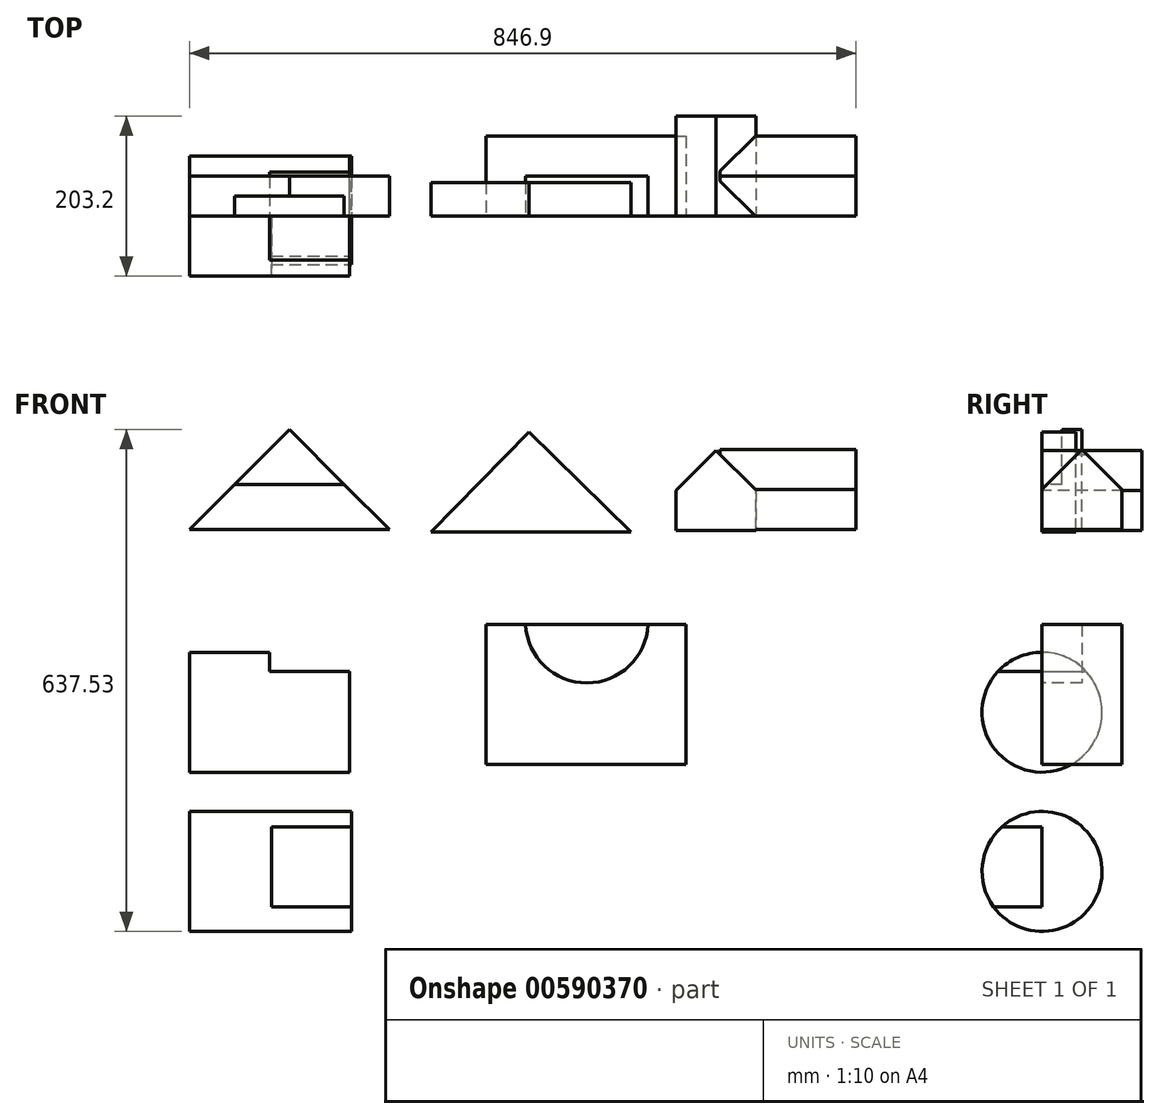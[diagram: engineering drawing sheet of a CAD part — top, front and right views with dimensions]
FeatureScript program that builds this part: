
annotation { "Feature Type Name" : "Feature", "Feature Type Description" : "" }
export const myFeature = defineFeature(function(context is Context, id is Id, definition is map)
    precondition{}
    {
        {
            var Q0;
            Q0=qCreatedBy(makeId("Front.planeOp"),FACE);
            var sketch = newSketch(context, id + "F0", { "sketchPlane" : qUnion([Q0])});
            skLineSegment(sketch, "E0", {"start": v(0, 0) * mm, "end": v(254, 0) * mm});
            skLineSegment(sketch, "E1", {"start": v(254, 0) * mm, "end": v(127, 127) * mm});
            skLineSegment(sketch, "E2", {"start": v(0, 0) * mm, "end": v(127, 127) * mm});
            skSolve(sketch);
        }
        {
            var Q0;
            Q0=makeQuery(id+"F0.imprint","IMPRINT",FACE,{"disambiguationData":[TD([[makeQuery(id+"F0.imprint","IMPRINT",EDGE,{"derivedFrom":sQuery(id+"F0.wireOp",EDGE,"E0")}),1.0]])]});
            extrude(context, id + "F1", {"entities" : qUnion([Q0]), "oppositeDirection" : true, "depth" : 50.8 * mm, "offsetDistance" : 25.4 * mm});
        }
        {
            var Q0;
            Q0=makeQuery(id+"F1.opExtrude","CAP_FACE",FACE,{"disambiguationData":[OSD([sQuery(id+"F0.wireOp",EDGE,"E0"),sQuery(id+"F0.wireOp",EDGE,"E1"),sQuery(id+"F0.wireOp",EDGE,"E2")])],"isStart":true});
            var sketch = newSketch(context, id + "F2", { "sketchPlane" : qUnion([Q0])});
            skLineSegment(sketch, "E3", {"start": v(57.32, 57.32) * mm, "end": v(196.68, 57.32) * mm});
            skSolve(sketch);
        }
        {
            var Q0;
            {var subQ0=sQuery(id+"F2.wireOp",EDGE,"E3");Q0=makeQuery(id+"F2.imprint","IMPRINT",FACE,{"disambiguationData":[TD([[makeQuery(id+"F2.imprint","IMPRINT",EDGE,{"derivedFrom":subQ0}),1.0]])]});}
            extrude(context, id + "F3", {"entities" : qUnion([Q0]), "operationType" : NewBodyOperationType.REMOVE, "oppositeDirection" : true, "depth" : 25.4 * mm, "offsetDistance" : 25.4 * mm});
        }
        {
            var Q0;
            Q0=qCreatedBy(makeId("Front.planeOp"),FACE);
            var sketch = newSketch(context, id + "F4", { "sketchPlane" : qUnion([Q0])});
            skLineSegment(sketch, "E4", {"start": v(307.02, -3.1) * mm, "end": v(561.02, -3.1) * mm});
            skLineSegment(sketch, "E5", {"start": v(307.02, -3.1) * mm, "end": v(431.46, 123.9) * mm});
            skLineSegment(sketch, "E6", {"start": v(561.02, -3.1) * mm, "end": v(431.46, 123.9) * mm});
            skSolve(sketch);
        }
        {
            var Q0;
            Q0=makeQuery(id+"F4.imprint","IMPRINT",FACE,{"disambiguationData":[TD([[makeQuery(id+"F4.imprint","IMPRINT",EDGE,{"derivedFrom":sQuery(id+"F4.wireOp",EDGE,"E4")}),1.0]])]});
            extrude(context, id + "F5", {"entities" : qUnion([Q0]), "oppositeDirection" : true, "depth" : 42.67 * mm, "offsetDistance" : 25.4 * mm});
        }
        {
            var Q0;
            Q0=qCreatedBy(makeId("Front.planeOp"),FACE);
            var sketch = newSketch(context, id + "F6", { "sketchPlane" : qUnion([Q0])});
            skLineSegment(sketch, "E7", {"start": v(618.3, -0.96) * mm, "end": v(618.3, 49.84) * mm});
            skLineSegment(sketch, "E8", {"start": v(618.3, 49.84) * mm, "end": v(669.1, 100.64) * mm});
            skLineSegment(sketch, "E9", {"start": v(669.1, 100.64) * mm, "end": v(719.9, 49.84) * mm});
            skLineSegment(sketch, "E10", {"start": v(719.9, 49.84) * mm, "end": v(719.9, -0.96) * mm});
            skLineSegment(sketch, "E11", {"start": v(719.9, -0.96) * mm, "end": v(618.3, -0.96) * mm});
            skSolve(sketch);
        }
        {
            var Q0;
            Q0=makeQuery(id+"F6.imprint","IMPRINT",FACE,{"disambiguationData":[TD([[makeQuery(id+"F6.imprint","IMPRINT",EDGE,{"derivedFrom":sQuery(id+"F6.wireOp",EDGE,"E7")}),-1.0]])]});
            extrude(context, id + "F7", {"entities" : qUnion([Q0]), "oppositeDirection" : true, "depth" : 127 * mm, "offsetDistance" : 25.4 * mm});
        }
        {
            var Q0;
            Q0=makeQuery(id+"F7.opExtrude","SWEPT_FACE",FACE,{"disambiguationData":[OSD([sQuery(id+"F6.wireOp",EDGE,"E10")])]});
            cPlane(context, id + "F8", {"entities" : qUnion([Q0]), "cplaneType" : CPlaneType.OFFSET, "offset" : 127 * mm, "width" : 152.4 * mm, "height" : 152.4 * mm});
        }
        {
            var Q0;
            Q0=qCreatedBy(id+"F8.planeOp",FACE);
            var sketch = newSketch(context, id + "F9", { "sketchPlane" : qUnion([Q0])});
            skLineSegment(sketch, "E12", {"start": v(0, 0) * mm, "end": v(101.6, 0) * mm});
            skLineSegment(sketch, "E13", {"start": v(101.6, 0) * mm, "end": v(101.6, 50.8) * mm});
            skLineSegment(sketch, "E14", {"start": v(101.6, 50.8) * mm, "end": v(50.8, 101.6) * mm});
            skLineSegment(sketch, "E15", {"start": v(0, 0) * mm, "end": v(0, 50.8) * mm});
            skLineSegment(sketch, "E16", {"start": v(0, 50.8) * mm, "end": v(50.8, 101.6) * mm});
            skSolve(sketch);
        }
        {
            var Q0;
            Q0=makeQuery(id+"F9.imprint","IMPRINT",FACE,{"disambiguationData":[TD([[makeQuery(id+"F9.imprint","IMPRINT",EDGE,{"derivedFrom":sQuery(id+"F9.wireOp",EDGE,"E12")}),1.0]])]});
            var Q1;
            Q1=makeQuery(id+"F7.opExtrude","SWEPT_FACE",FACE,{"disambiguationData":[OSD([sQuery(id+"F6.wireOp",EDGE,"E10")])]});
            extrude(context, id + "F10", {"entities" : qUnion([Q0]), "operationType" : NewBodyOperationType.ADD, "endBound" : BoundingType.UP_TO_SURFACE, "oppositeDirection" : true, "depth" : 165.1 * mm, "endBoundEntityFace" : qUnion([Q1]), "offsetDistance" : 25.4 * mm});
        }
        {
            var Q0;
            Q0=makeQuery(id+"F10.opExtrude","CAP_FACE",FACE,{"disambiguationData":[OSD([sQuery(id+"F9.wireOp",EDGE,"E12"),sQuery(id+"F9.wireOp",EDGE,"E13"),sQuery(id+"F9.wireOp",EDGE,"E14"),sQuery(id+"F9.wireOp",EDGE,"E15"),sQuery(id+"F9.wireOp",EDGE,"E16")])],"isStart":false});
            extrude(context, id + "F11", {"entities" : qUnion([Q0]), "operationType" : NewBodyOperationType.ADD, "depth" : 45.72 * mm, "offsetDistance" : 25.4 * mm});
        }
        {
            var Q0;
            Q0=qCreatedBy(makeId("Right.planeOp"),FACE);
            var sketch = newSketch(context, id + "F12", { "sketchPlane" : qUnion([Q0])});
            skCircle(sketch, "E17", {"center": v(0, -232.1) * mm, "radius": 76.2 * mm});
            skSolve(sketch);
        }
        {
            var Q0;
            Q0=makeQuery(id+"F12.imprint","IMPRINT",FACE,{"disambiguationData":[TD([[makeQuery(id+"F12.imprint","IMPRINT",EDGE,{"derivedFrom":sQuery(id+"F12.wireOp",EDGE,"E17")}),1.0]])]});
            var Q1;
            Q1=sQuery(id+"F12.wireOp",EDGE,"E17");
            extrude(context, id + "F13", {"entities" : qUnion([Q0]), "surfaceEntities" : qUnion([Q1]), "depth" : 203.2 * mm, "offsetDistance" : 25.4 * mm});
        }
        {
            var Q0;
            Q0=makeQuery(id+"F13.opExtrude","CAP_FACE",FACE,{"disambiguationData":[OSD([sQuery(id+"F12.wireOp",EDGE,"E17")])],"isStart":false});
            var sketch = newSketch(context, id + "F14", { "sketchPlane" : qUnion([Q0])});
            skLineSegment(sketch, "E18", {"start": v(-55.8, -180.2) * mm, "end": v(55.8, -180.2) * mm});
            skSolve(sketch);
        }
        {
            var Q0;
            {var subQ0=sQuery(id+"F14.wireOp",EDGE,"E18");Q0=makeQuery(id+"F14.imprint","IMPRINT",FACE,{"disambiguationData":[TD([[makeQuery(id+"F14.imprint","IMPRINT",EDGE,{"derivedFrom":subQ0}),1.0]])]});}
            extrude(context, id + "F15", {"entities" : qUnion([Q0]), "operationType" : NewBodyOperationType.REMOVE, "oppositeDirection" : true, "depth" : 101.6 * mm, "offsetDistance" : 25.4 * mm});
        }
        {
            var Q0;
            Q0=qCreatedBy(makeId("Right.planeOp"),FACE);
            var sketch = newSketch(context, id + "F16", { "sketchPlane" : qUnion([Q0])});
            skCircle(sketch, "E19", {"center": v(0, -434.33) * mm, "radius": 76.2 * mm});
            skSolve(sketch);
        }
        {
            var Q0;
            Q0=makeQuery(id+"F16.imprint","IMPRINT",FACE,{"disambiguationData":[TD([[makeQuery(id+"F16.imprint","IMPRINT",EDGE,{"derivedFrom":sQuery(id+"F16.wireOp",EDGE,"E19")}),1.0]])]});
            extrude(context, id + "F17", {"entities" : qUnion([Q0]), "depth" : 205.74 * mm, "offsetDistance" : 25.4 * mm});
        }
        {
            var Q0;
            Q0=makeQuery(id+"F17.opExtrude","CAP_FACE",FACE,{"disambiguationData":[OSD([sQuery(id+"F16.wireOp",EDGE,"E19")])],"isStart":false});
            var sketch = newSketch(context, id + "F18", { "sketchPlane" : qUnion([Q0])});
            skLineSegment(sketch, "E20", {"start": v(-50.8, -377.53) * mm, "end": v(0, -377.53) * mm});
            skLineSegment(sketch, "E21", {"start": v(0, -377.53) * mm, "end": v(0, -479.13) * mm});
            skLineSegment(sketch, "E22", {"start": v(0, -479.13) * mm, "end": v(-61.64, -479.13) * mm});
            skSolve(sketch);
        }
        {
            var Q0;
            {var subQ0=sQuery(id+"F18.wireOp",EDGE,"E20");Q0=makeQuery(id+"F18.imprint","IMPRINT",FACE,{"disambiguationData":[TD([[makeQuery(id+"F18.imprint","IMPRINT",EDGE,{"derivedFrom":subQ0}),-1.0]])]});}
            extrude(context, id + "F19", {"entities" : qUnion([Q0]), "operationType" : NewBodyOperationType.REMOVE, "oppositeDirection" : true, "depth" : 101.6 * mm, "offsetDistance" : 25.4 * mm});
        }
        {
            var Q0;
            Q0=qCreatedBy(makeId("Front.planeOp"),FACE);
            var sketch = newSketch(context, id + "F20", { "sketchPlane" : qUnion([Q0])});
            skLineSegment(sketch, "E23", {"start": v(376.77, -120.87) * mm, "end": v(376.77, -298.67) * mm});
            skLineSegment(sketch, "E24", {"start": v(376.77, -298.67) * mm, "end": v(630.77, -298.67) * mm});
            skLineSegment(sketch, "E25", {"start": v(630.77, -298.67) * mm, "end": v(630.77, -120.87) * mm});
            skLineSegment(sketch, "E26", {"start": v(376.77, -120.87) * mm, "end": v(630.77, -120.87) * mm});
            skSolve(sketch);
        }
        {
            var Q0;
            Q0=makeQuery(id+"F20.imprint","IMPRINT",FACE,{"disambiguationData":[TD([[makeQuery(id+"F20.imprint","IMPRINT",EDGE,{"derivedFrom":sQuery(id+"F20.wireOp",EDGE,"E23")}),1.0]])]});
            extrude(context, id + "F21", {"entities" : qUnion([Q0]), "oppositeDirection" : true, "depth" : 101.6 * mm, "offsetDistance" : 25.4 * mm});
        }
        {
            var Q0;
            Q0=makeQuery(id+"F20.imprint","IMPRINT",FACE,{"disambiguationData":[TD([[makeQuery(id+"F20.imprint","IMPRINT",EDGE,{"derivedFrom":sQuery(id+"F20.wireOp",EDGE,"E23")}),1.0]])]});
            var sketch = newSketch(context, id + "F22", { "sketchPlane" : qUnion([Q0])});
            skCircle(sketch, "E27", {"center": v(504.89, -116.85) * mm, "radius": 78.03 * mm});
            skSolve(sketch);
        }
        {
            var Q0;
            {var subQ0=sQuery(id+"F22.wireOp",EDGE,"E27");var subQ1=makeQuery(id+"F20.imprint","IMPRINT",EDGE,{"derivedFrom":sQuery(id+"F20.wireOp",EDGE,"E26")});var subQ2=makeQuery(id+"F22.imprint","INTERSECT",VERTEX,{"disambiguationData":[OD(0.0)],"derivedFrom":[subQ1,subQ0]});Q0=makeQuery(id+"F22.imprint","IMPRINT",FACE,{"disambiguationData":[TD([[makeQuery(id+"F22.imprint","IMPRINT",EDGE,{"disambiguationData":[TD([[subQ2,-1.0]])],"derivedFrom":subQ0}),1.0]])]});}
            extrude(context, id + "F23", {"entities" : qUnion([Q0]), "operationType" : NewBodyOperationType.REMOVE, "oppositeDirection" : true, "depth" : 50.8 * mm, "offsetDistance" : 25.4 * mm});
        }
    });
